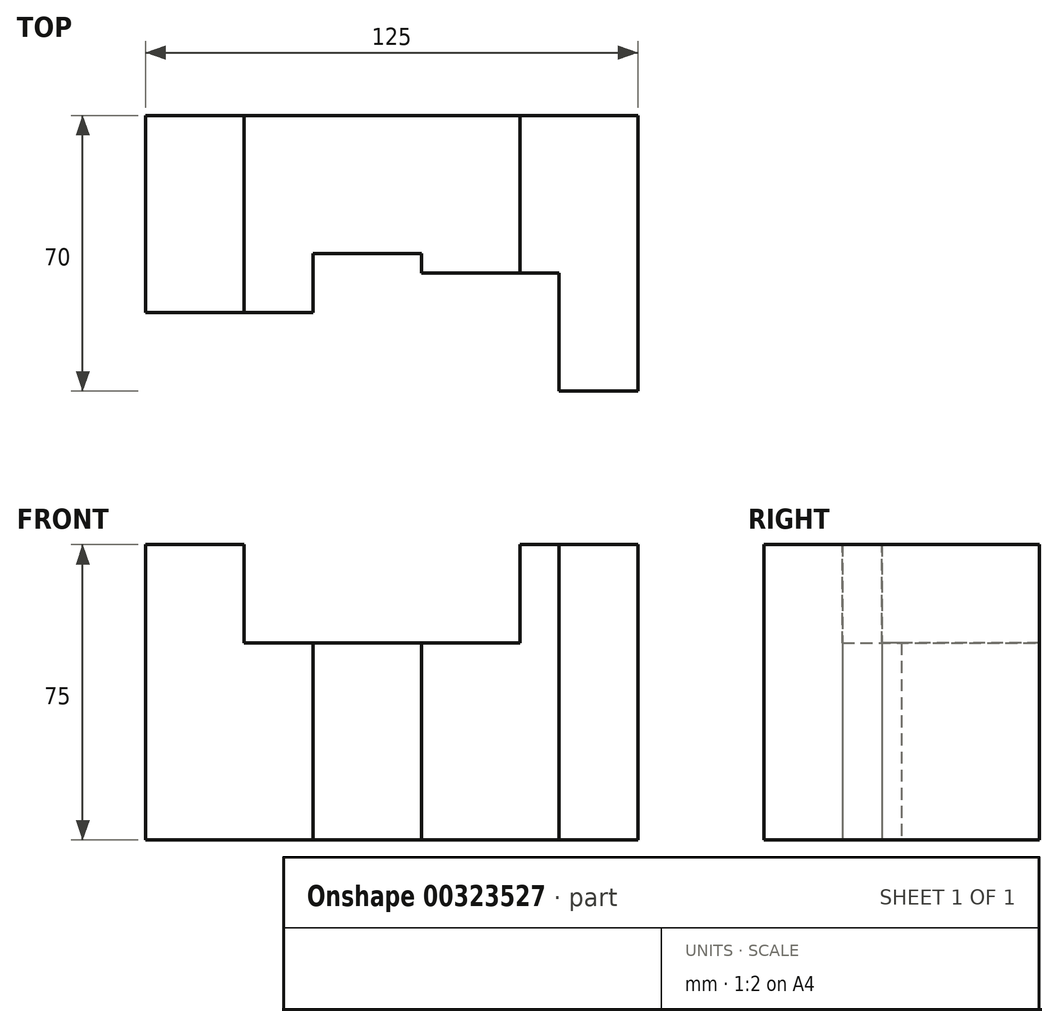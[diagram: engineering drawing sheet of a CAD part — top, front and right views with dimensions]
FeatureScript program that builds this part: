
annotation { "Feature Type Name" : "Feature", "Feature Type Description" : "" }
export const myFeature = defineFeature(function(context is Context, id is Id, definition is map)
    precondition{}
    {
        {
            var Q0;
            Q0=qCreatedBy(makeId("Top.planeOp"),FACE);
            var sketch = newSketch(context, id + "F0", { "sketchPlane" : qUnion([Q0])});
            skLineSegment(sketch, "E0", {"start": v(0, 0) * mm, "end": v(42.5, 0) * mm});
            skLineSegment(sketch, "E1", {"start": v(42.5, 0) * mm, "end": v(42.5, 15) * mm});
            skLineSegment(sketch, "E2", {"start": v(42.5, 15) * mm, "end": v(70, 15) * mm});
            skLineSegment(sketch, "E3", {"start": v(70, 15) * mm, "end": v(70, 10) * mm});
            skLineSegment(sketch, "E4", {"start": v(70, 10) * mm, "end": v(105, 10) * mm});
            skLineSegment(sketch, "E5", {"start": v(105, 10) * mm, "end": v(105, -20) * mm});
            skLineSegment(sketch, "E6", {"start": v(105, -20) * mm, "end": v(125, -20) * mm});
            skLineSegment(sketch, "E7", {"start": v(125, -20) * mm, "end": v(125, 50) * mm});
            skLineSegment(sketch, "E8", {"start": v(125, 50) * mm, "end": v(0, 50) * mm});
            skLineSegment(sketch, "E9", {"start": v(0, 50) * mm, "end": v(0, 0) * mm});
            skLineSegment(sketch, "E10", {"start": v(25, 0) * mm, "end": v(25, 50) * mm});
            skLineSegment(sketch, "E11", {"start": v(95, 10) * mm, "end": v(95, 50) * mm});
            skSolve(sketch);
        }
        {
            var Q0;
            Q0 = qSketchRegion(id + "F0", true);
            extrude(context, id + "F1", {"entities" : qUnion([Q0]), "depth" : 75 * mm});
        }
        {
            var Q0;
            Q0=makeQuery(id+"F1.opExtrude","CAP_FACE",FACE,{"disambiguationData":[OSD([sQuery(id+"F0.wireOp",EDGE,"E0"),sQuery(id+"F0.wireOp",EDGE,"E1"),sQuery(id+"F0.wireOp",EDGE,"E2"),sQuery(id+"F0.wireOp",EDGE,"E3"),sQuery(id+"F0.wireOp",EDGE,"E4"),sQuery(id+"F0.wireOp",EDGE,"E5"),sQuery(id+"F0.wireOp",EDGE,"E6"),sQuery(id+"F0.wireOp",EDGE,"E7"),sQuery(id+"F0.wireOp",EDGE,"E8"),sQuery(id+"F0.wireOp",EDGE,"E9")])],"isStart":false});
            var sketch = newSketch(context, id + "F2", { "sketchPlane" : qUnion([Q0])});
            skLineSegment(sketch, "E12", {"start": v(95, 50) * mm, "end": v(95, 10) * mm});
            skLineSegment(sketch, "E13", {"start": v(95, 10) * mm, "end": v(70, 10) * mm});
            skLineSegment(sketch, "E14", {"start": v(70, 10) * mm, "end": v(70, 15) * mm});
            skLineSegment(sketch, "E15", {"start": v(70, 15) * mm, "end": v(42.5, 15) * mm});
            skLineSegment(sketch, "E16", {"start": v(42.5, 15) * mm, "end": v(42.5, 0) * mm});
            skLineSegment(sketch, "E17", {"start": v(42.5, 0) * mm, "end": v(25, 0) * mm});
            skLineSegment(sketch, "E18", {"start": v(25, 0) * mm, "end": v(25, 50) * mm});
            skLineSegment(sketch, "E19", {"start": v(25, 50) * mm, "end": v(95, 50) * mm});
            skSolve(sketch);
        }
        {
            var Q0;
            Q0=makeQuery(id+"F2.imprint","IMPRINT",FACE,{"disambiguationData":[TD([[makeQuery(id+"F2.imprint","IMPRINT",EDGE,{"derivedFrom":sQuery(id+"F2.wireOp",EDGE,"E12")}),-1.0]])]});
            extrude(context, id + "F3", {"entities" : qUnion([Q0]), "operationType" : NewBodyOperationType.REMOVE, "oppositeDirection" : true, "depth" : 25 * mm});
        }
    });
